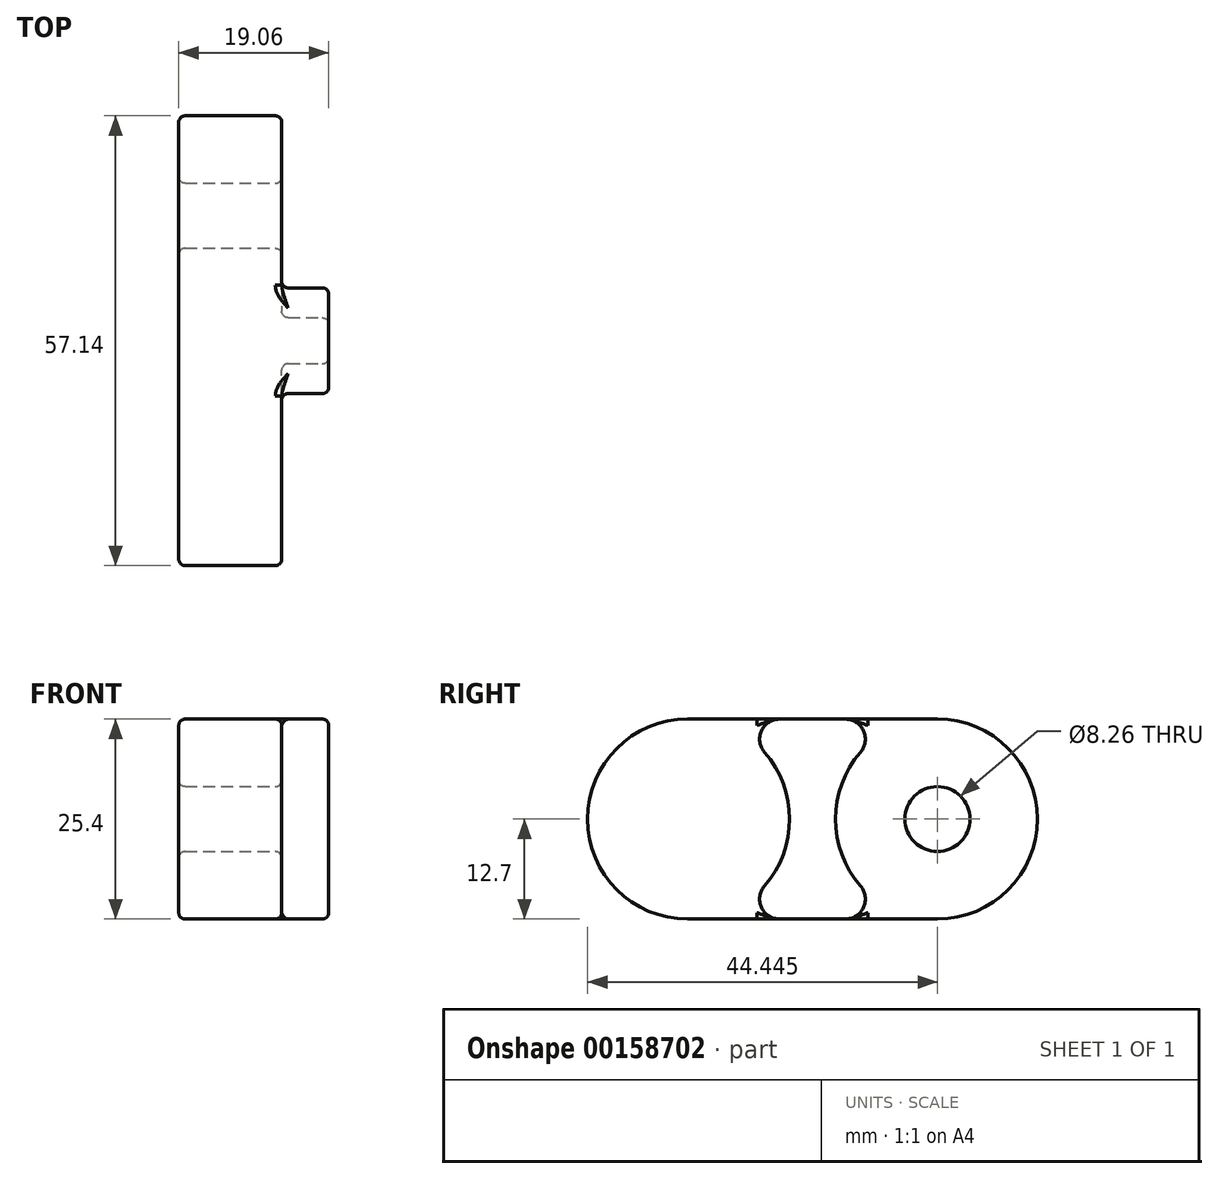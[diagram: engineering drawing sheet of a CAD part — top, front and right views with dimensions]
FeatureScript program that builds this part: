
annotation { "Feature Type Name" : "Feature", "Feature Type Description" : "" }
export const myFeature = defineFeature(function(context is Context, id is Id, definition is map)
    precondition{}
    {
        {
            var Q0;
            Q0=qCreatedBy(makeId("Right.planeOp"),FACE);
            var sketch = newSketch(context, id + "F0", { "sketchPlane" : qUnion([Q0])});
            skLineSegment(sketch, "E0", {"start": v(-15.88, 0) * mm, "end": v(15.88, 0) * mm, "construction": true});
            skArc(sketch, "E1.0.startCap", {"start": v(-15.88, -12.7) * mm, "mid": v(-28.58, 0) * mm, "end": v(-15.87, 12.7) * mm});
            skArc(sketch, "E1.0.endCap", {"start": v(15.88, 12.7) * mm, "mid": v(28.58, 0) * mm, "end": v(15.88, -12.7) * mm});
            skLineSegment(sketch, "E1.0.left", {"start": v(-15.88, 12.7) * mm, "end": v(15.88, 12.7) * mm});
            skLineSegment(sketch, "E1.0.right", {"start": v(-15.88, -12.7) * mm, "end": v(15.88, -12.7) * mm});
            skSolve(sketch);
        }
        {
            var Q0;
            Q0 = qSketchRegion(id + "F0", true);
            extrude(context, id + "F1", {"entities" : qUnion([Q0]), "endBound" : BoundingType.SYMMETRIC, "depth" : 19.05 * mm});
        }
        {
            var Q0;
            Q0=makeQuery(id+"F1.opExtrude","CAP_FACE",FACE,{"disambiguationData":[OSD([sQuery(id+"F0.wireOp",EDGE,"E1.0.startCap"),sQuery(id+"F0.wireOp",EDGE,"E1.0.endCap"),sQuery(id+"F0.wireOp",EDGE,"E1.0.left"),sQuery(id+"F0.wireOp",EDGE,"E1.0.right")])],"isStart":false});
            var sketch = newSketch(context, id + "F2", { "sketchPlane" : qUnion([Q0])});
            skCircle(sketch, "E2", {"center": v(-15.88, 0) * mm, "radius": 12.95 * mm});
            skCircle(sketch, "E3", {"center": v(15.88, 0) * mm, "radius": 12.95 * mm});
            skSolve(sketch);
        }
        {
            var Q0;
            Q0 = qSketchRegion(id + "F2", true);
            extrude(context, id + "F3", {"entities" : qUnion([Q0]), "operationType" : NewBodyOperationType.REMOVE, "oppositeDirection" : true, "depth" : 5.97 * mm});
        }
        {
            var Q0;
            Q0=makeQuery(id+"F3.boolean.opBoolean","COPY",FACE,{"derivedFrom":makeQuery(id+"F3.opExtrude","CAP_FACE",FACE,{"disambiguationData":[OSD([sQuery(id+"F2.wireOp",EDGE,"E3")])],"isStart":false})});
            var sketch = newSketch(context, id + "F4", { "sketchPlane" : qUnion([Q0])});
            skCircle(sketch, "E4", {"center": v(15.88, 0) * mm, "radius": 4.13 * mm});
            skCircle(sketch, "E5.MirrorC", {"center": v(-15.88, 0) * mm, "radius": 4.13 * mm});
            skSolve(sketch);
        }
        {
            var Q0;
            Q0=makeQuery(id+"F4.imprint","IMPRINT",FACE,{"disambiguationData":[TD([[makeQuery(id+"F4.imprint","IMPRINT",EDGE,{"derivedFrom":sQuery(id+"F4.wireOp",EDGE,"E4")}),1.0]])]});
            var Q1;
            Q1=makeQuery(id+"F4.imprint","IMPRINT",FACE,{"disambiguationData":[TD([[makeQuery(id+"F4.imprint","IMPRINT",EDGE,{"derivedFrom":sQuery(id+"F4.wireOp",EDGE,"E5.MirrorC")}),-1.0]])]});
            var Q2;
            Q2=sQuery(id+"F4.wireOp",EDGE,"E4");
            var Q3;
            Q3=sQuery(id+"F4.wireOp",EDGE,"E5.MirrorC");
            extrude(context, id + "F5", {"entities" : qUnion([Q0, Q1]), "operationType" : NewBodyOperationType.REMOVE, "surfaceEntities" : qUnion([Q2, Q3]), "endBound" : BoundingType.THROUGH_ALL, "oppositeDirection" : true, "depth" : 25.4 * mm});
        }
        {
            var Q0;
            Q0=makeQuery(id+"F3.boolean.opBoolean","INTERSECT",EDGE,{"derivedFrom":[makeQuery(id+"F1.opExtrude","SWEPT_FACE",FACE,{"disambiguationData":[OSD([sQuery(id+"F0.wireOp",EDGE,"E1.0.left")])]}),makeQuery(id+"F3.opExtrude","SWEPT_FACE",FACE,{"disambiguationData":[OSD([sQuery(id+"F2.wireOp",EDGE,"E3")])]})]});
            var Q1;
            Q1=makeQuery(id+"FXmAiSPnTKzVYhG_1.1.F3.boolean.opBoolean","INTERSECT",EDGE,{"derivedFrom":[makeQuery(id+"F1.opExtrude","SWEPT_FACE",FACE,{"disambiguationData":[OSD([sQuery(id+"F0.wireOp",EDGE,"E1.0.left")])]}),makeQuery(id+"FXmAiSPnTKzVYhG_1.1.F3.opExtrude","SWEPT_FACE",FACE,{"disambiguationData":[OSD([sQuery(id+"F2.wireOp",EDGE,"E3")])]})]});
            var Q2;
            Q2=makeQuery(id+"F3.boolean.opBoolean","INTERSECT",EDGE,{"derivedFrom":[makeQuery(id+"F1.opExtrude","SWEPT_FACE",FACE,{"disambiguationData":[OSD([sQuery(id+"F0.wireOp",EDGE,"E1.0.left")])]}),makeQuery(id+"F3.opExtrude","SWEPT_FACE",FACE,{"disambiguationData":[OSD([sQuery(id+"F2.wireOp",EDGE,"E2")])]})]});
            var Q3;
            Q3=makeQuery(id+"FXmAiSPnTKzVYhG_1.1.F3.boolean.opBoolean","INTERSECT",EDGE,{"derivedFrom":[makeQuery(id+"F1.opExtrude","SWEPT_FACE",FACE,{"disambiguationData":[OSD([sQuery(id+"F0.wireOp",EDGE,"E1.0.left")])]}),makeQuery(id+"FXmAiSPnTKzVYhG_1.1.F3.opExtrude","SWEPT_FACE",FACE,{"disambiguationData":[OSD([sQuery(id+"F2.wireOp",EDGE,"E2")])]})]});
            var Q4;
            Q4=makeQuery(id+"F3.boolean.opBoolean","INTERSECT",EDGE,{"derivedFrom":[makeQuery(id+"F1.opExtrude","SWEPT_FACE",FACE,{"disambiguationData":[OSD([sQuery(id+"F0.wireOp",EDGE,"E1.0.right")])]}),makeQuery(id+"F3.opExtrude","SWEPT_FACE",FACE,{"disambiguationData":[OSD([sQuery(id+"F2.wireOp",EDGE,"E3")])]})]});
            var Q5;
            Q5=makeQuery(id+"F3.boolean.opBoolean","INTERSECT",EDGE,{"derivedFrom":[makeQuery(id+"F1.opExtrude","SWEPT_FACE",FACE,{"disambiguationData":[OSD([sQuery(id+"F0.wireOp",EDGE,"E1.0.right")])]}),makeQuery(id+"F3.opExtrude","SWEPT_FACE",FACE,{"disambiguationData":[OSD([sQuery(id+"F2.wireOp",EDGE,"E2")])]})]});
            var Q6;
            Q6=makeQuery(id+"FXmAiSPnTKzVYhG_1.1.F3.boolean.opBoolean","INTERSECT",EDGE,{"derivedFrom":[makeQuery(id+"F1.opExtrude","SWEPT_FACE",FACE,{"disambiguationData":[OSD([sQuery(id+"F0.wireOp",EDGE,"E1.0.right")])]}),makeQuery(id+"FXmAiSPnTKzVYhG_1.1.F3.opExtrude","SWEPT_FACE",FACE,{"disambiguationData":[OSD([sQuery(id+"F2.wireOp",EDGE,"E3")])]})]});
            var Q7;
            Q7=makeQuery(id+"FXmAiSPnTKzVYhG_1.1.F3.boolean.opBoolean","INTERSECT",EDGE,{"derivedFrom":[makeQuery(id+"F1.opExtrude","SWEPT_FACE",FACE,{"disambiguationData":[OSD([sQuery(id+"F0.wireOp",EDGE,"E1.0.right")])]}),makeQuery(id+"FXmAiSPnTKzVYhG_1.1.F3.opExtrude","SWEPT_FACE",FACE,{"disambiguationData":[OSD([sQuery(id+"F2.wireOp",EDGE,"E2")])]})]});
            fillet(context, id + "F6", {"entities" : qUnion([Q0, Q1, Q2, Q3, Q4, Q5, Q6, Q7]), "radius" : 2.54 * mm, "tangentPropagation" : true, "allowEdgeOverflow" : false});
        }
        {
            var Q0;
            Q0=makeQuery(id+"FXmAiSPnTKzVYhG_1.1.F3.boolean.opBoolean","COPY",FACE,{"derivedFrom":makeQuery(id+"FXmAiSPnTKzVYhG_1.1.F3.opExtrude","CAP_FACE",FACE,{"disambiguationData":[OSD([sQuery(id+"F2.wireOp",EDGE,"E3")])],"isStart":false})});
            var Q1;
            Q1=makeQuery(id+"FXmAiSPnTKzVYhG_1.1.F3.boolean.opBoolean","COPY",FACE,{"derivedFrom":makeQuery(id+"FXmAiSPnTKzVYhG_1.1.F3.opExtrude","CAP_FACE",FACE,{"disambiguationData":[OSD([sQuery(id+"F2.wireOp",EDGE,"E2")])],"isStart":false})});
            var Q2;
            Q2=makeQuery(id+"F3.boolean.opBoolean","COPY",FACE,{"derivedFrom":makeQuery(id+"F3.opExtrude","CAP_FACE",FACE,{"disambiguationData":[OSD([sQuery(id+"F2.wireOp",EDGE,"E2")])],"isStart":false})});
            var Q3;
            Q3=makeQuery(id+"F3.boolean.opBoolean","COPY",FACE,{"derivedFrom":makeQuery(id+"F3.opExtrude","CAP_FACE",FACE,{"disambiguationData":[OSD([sQuery(id+"F2.wireOp",EDGE,"E3")])],"isStart":false})});
            var Q4;
            Q4=makeQuery(id+"F1.opExtrude","CAP_FACE",FACE,{"disambiguationData":[OSD([sQuery(id+"F0.wireOp",EDGE,"E1.0.startCap"),sQuery(id+"F0.wireOp",EDGE,"E1.0.endCap"),sQuery(id+"F0.wireOp",EDGE,"E1.0.left"),sQuery(id+"F0.wireOp",EDGE,"E1.0.right")])],"isStart":true});
            var Q5;
            Q5=makeQuery(id+"F1.opExtrude","CAP_FACE",FACE,{"disambiguationData":[OSD([sQuery(id+"F0.wireOp",EDGE,"E1.0.startCap"),sQuery(id+"F0.wireOp",EDGE,"E1.0.endCap"),sQuery(id+"F0.wireOp",EDGE,"E1.0.left"),sQuery(id+"F0.wireOp",EDGE,"E1.0.right")])],"isStart":false});
            fillet(context, id + "F7", {"entities" : qUnion([Q0, Q1, Q2, Q3, Q4, Q5]), "radius" : 0.81 * mm, "tangentPropagation" : true, "allowEdgeOverflow" : false});
        }
    });
